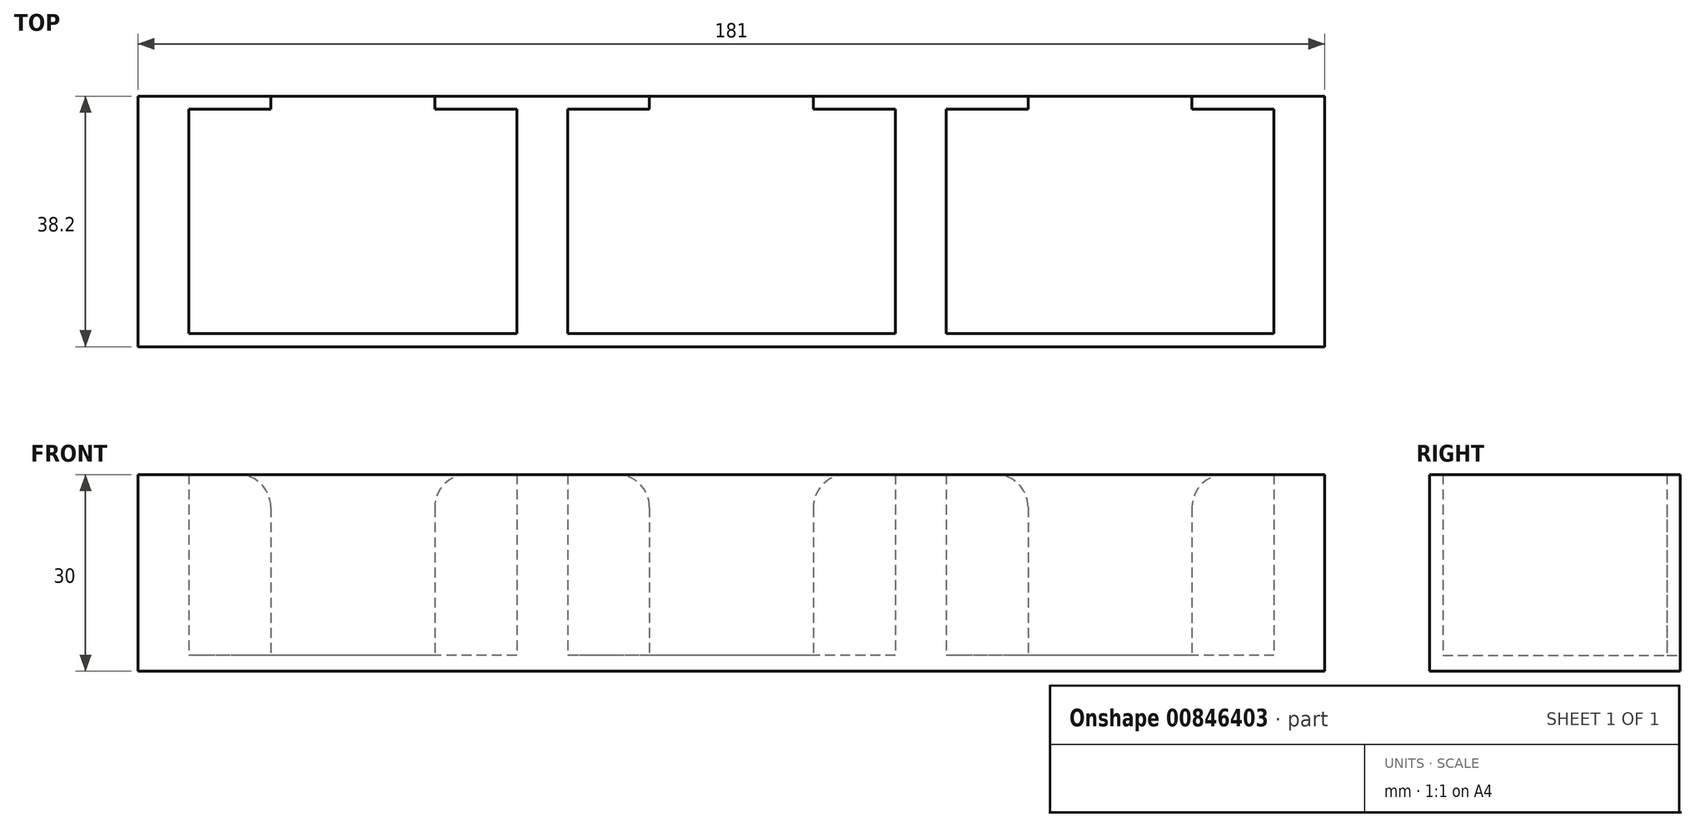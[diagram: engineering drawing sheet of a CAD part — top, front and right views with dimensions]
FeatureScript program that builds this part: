
annotation { "Feature Type Name" : "Feature", "Feature Type Description" : "" }
export const myFeature = defineFeature(function(context is Context, id is Id, definition is map)
    precondition{}
    {
        {
            var Q0;
            Q0=qCreatedBy(makeId("Top.planeOp"),FACE);
            var sketch = newSketch(context, id + "F0", { "sketchPlane" : qUnion([Q0])});
            skPoint(sketch, "E0.middle", {"position": v(0, 0) * mm});
            skLineSegment(sketch, "E1.bottom", {"start": v(90.5, -19.1) * mm, "end": v(-90.5, -19.1) * mm});
            skLineSegment(sketch, "E1.top", {"start": v(90.5, 19.1) * mm, "end": v(-90.5, 19.1) * mm});
            skLineSegment(sketch, "E1.left", {"start": v(90.5, -19.5) * mm, "end": v(90.5, 19.5) * mm});
            skLineSegment(sketch, "E1.right", {"start": v(-90.5, -19.5) * mm, "end": v(-90.5, 19.5) * mm});
            skLineSegment(sketch, "E2.0", {"start": v(88.1, 17.1) * mm, "end": v(-88.1, 17.1) * mm});
            skLineSegment(sketch, "E2.2", {"start": v(88.1, -17.1) * mm, "end": v(-88.1, -17.1) * mm});
            skLineSegment(sketch, "E3.0", {"start": v(82.75, -17.1) * mm, "end": v(82.75, 17.1) * mm});
            skLineSegment(sketch, "E4.0", {"start": v(-82.75, -17.1) * mm, "end": v(-82.75, 17.1) * mm});
            skLineSegment(sketch, "E5.0", {"start": v(-32.75, -17.1) * mm, "end": v(-32.75, 17.1) * mm});
            skLineSegment(sketch, "E6.0", {"start": v(32.75, -17.1) * mm, "end": v(32.75, 17.1) * mm});
            skLineSegment(sketch, "E7.0", {"start": v(-25, -17.1) * mm, "end": v(-25, 17.1) * mm});
            skLineSegment(sketch, "E8.0", {"start": v(25, -17.1) * mm, "end": v(25, 17.1) * mm});
            skLineSegment(sketch, "E9.0", {"start": v(-70.25, -19.5) * mm, "end": v(-70.25, 19.5) * mm});
            skLineSegment(sketch, "E10.0", {"start": v(-45.25, -19.5) * mm, "end": v(-45.25, 19.5) * mm});
            skLineSegment(sketch, "E11.0", {"start": v(-12.5, -19.5) * mm, "end": v(-12.5, 19.5) * mm});
            skLineSegment(sketch, "E12.0", {"start": v(12.5, -19.5) * mm, "end": v(12.5, 19.5) * mm});
            skLineSegment(sketch, "E13.0", {"start": v(45.25, -19.5) * mm, "end": v(45.25, 19.5) * mm});
            skLineSegment(sketch, "E14.0", {"start": v(70.25, -19.5) * mm, "end": v(70.25, 19.5) * mm});
            skSolve(sketch);
        }
        {
            var Q0;
            {var subQ0=sQuery(id+"F0.wireOp",EDGE,"E1.right");Q0=makeQuery(id+"F0.imprint","IMPRINT",FACE,{"disambiguationData":[TD([[makeQuery(id+"F0.imprint","IMPRINT",EDGE,{"derivedFrom":subQ0}),-1.0]])]});}
            var Q1;
            {var subQ0=sQuery(id+"F0.wireOp",EDGE,"E9.0");var subQ1=sQuery(id+"F0.wireOp",EDGE,"E1.bottom");var subQ2=makeQuery(id+"F0.imprint","INTERSECT",VERTEX,{"derivedFrom":[subQ1,subQ0]});Q1=makeQuery(id+"F0.imprint","IMPRINT",FACE,{"disambiguationData":[TD([[makeQuery(id+"F0.imprint","IMPRINT",EDGE,{"disambiguationData":[TD([[subQ2,1.0]])],"derivedFrom":subQ1}),-1.0]])]});}
            var Q2;
            {var subQ2=sQuery(id+"F0.wireOp",EDGE,"E10.0");var subQ7=sQuery(id+"F0.wireOp",EDGE,"E1.bottom");var subQ8=makeQuery(id+"F0.imprint","INTERSECT",VERTEX,{"derivedFrom":[subQ7,subQ2]});Q2=makeQuery(id+"F0.imprint","IMPRINT",FACE,{"disambiguationData":[TD([[makeQuery(id+"F0.imprint","IMPRINT",EDGE,{"disambiguationData":[TD([[subQ8,1.0]])],"derivedFrom":subQ7}),-1.0]])]});}
            var Q3;
            {var subQ2=sQuery(id+"F0.wireOp",EDGE,"E10.0");var subQ7=sQuery(id+"F0.wireOp",EDGE,"E1.top");var subQ8=makeQuery(id+"F0.imprint","INTERSECT",VERTEX,{"derivedFrom":[subQ7,subQ2]});Q3=makeQuery(id+"F0.imprint","IMPRINT",FACE,{"disambiguationData":[TD([[makeQuery(id+"F0.imprint","IMPRINT",EDGE,{"disambiguationData":[TD([[subQ8,1.0]])],"derivedFrom":subQ7}),1.0]])]});}
            var Q4;
            {var subQ0=sQuery(id+"F0.wireOp",EDGE,"E11.0");var subQ1=sQuery(id+"F0.wireOp",EDGE,"E1.bottom");var subQ2=makeQuery(id+"F0.imprint","INTERSECT",VERTEX,{"derivedFrom":[subQ1,subQ0]});Q4=makeQuery(id+"F0.imprint","IMPRINT",FACE,{"disambiguationData":[TD([[makeQuery(id+"F0.imprint","IMPRINT",EDGE,{"disambiguationData":[TD([[subQ2,1.0]])],"derivedFrom":subQ1}),-1.0]])]});}
            var Q5;
            {var subQ2=sQuery(id+"F0.wireOp",EDGE,"E12.0");var subQ4=sQuery(id+"F0.wireOp",EDGE,"E1.bottom");var subQ5=makeQuery(id+"F0.imprint","INTERSECT",VERTEX,{"derivedFrom":[subQ4,subQ2]});Q5=makeQuery(id+"F0.imprint","IMPRINT",FACE,{"disambiguationData":[TD([[makeQuery(id+"F0.imprint","IMPRINT",EDGE,{"disambiguationData":[TD([[subQ5,1.0]])],"derivedFrom":subQ4}),-1.0]])]});}
            var Q6;
            {var subQ0=sQuery(id+"F0.wireOp",EDGE,"E13.0");var subQ1=sQuery(id+"F0.wireOp",EDGE,"E1.bottom");var subQ2=makeQuery(id+"F0.imprint","INTERSECT",VERTEX,{"derivedFrom":[subQ1,subQ0]});Q6=makeQuery(id+"F0.imprint","IMPRINT",FACE,{"disambiguationData":[TD([[makeQuery(id+"F0.imprint","IMPRINT",EDGE,{"disambiguationData":[TD([[subQ2,1.0]])],"derivedFrom":subQ1}),-1.0]])]});}
            var Q7;
            {var subQ6=sQuery(id+"F0.wireOp",EDGE,"E1.left");Q7=makeQuery(id+"F0.imprint","IMPRINT",FACE,{"disambiguationData":[TD([[makeQuery(id+"F0.imprint","IMPRINT",EDGE,{"derivedFrom":subQ6}),1.0]])]});}
            var Q8;
            {var subQ2=sQuery(id+"F0.wireOp",EDGE,"E12.0");var subQ4=sQuery(id+"F0.wireOp",EDGE,"E1.top");var subQ5=makeQuery(id+"F0.imprint","INTERSECT",VERTEX,{"derivedFrom":[subQ4,subQ2]});Q8=makeQuery(id+"F0.imprint","IMPRINT",FACE,{"disambiguationData":[TD([[makeQuery(id+"F0.imprint","IMPRINT",EDGE,{"disambiguationData":[TD([[subQ5,1.0]])],"derivedFrom":subQ4}),1.0]])]});}
            var Q9;
            {var subQ0=sQuery(id+"F0.wireOp",EDGE,"E6.0");Q9=makeQuery(id+"F0.imprint","IMPRINT",FACE,{"disambiguationData":[TD([[makeQuery(id+"F0.imprint","IMPRINT",EDGE,{"derivedFrom":subQ0}),1.0]])]});}
            var Q10;
            {var subQ0=sQuery(id+"F0.wireOp",EDGE,"E5.0");Q10=makeQuery(id+"F0.imprint","IMPRINT",FACE,{"disambiguationData":[TD([[makeQuery(id+"F0.imprint","IMPRINT",EDGE,{"derivedFrom":subQ0}),-1.0]])]});}
            extrude(context, id + "F1", {"entities" : qUnion([Q0, Q1, Q2, Q3, Q4, Q5, Q6, Q7, Q8, Q9, Q10]), "depth" : 30 * mm, "offsetDistance" : 25 * mm});
        }
        {
            var Q0;
            {var subQ0=sQuery(id+"F0.wireOp",EDGE,"E9.0");var subQ1=sQuery(id+"F0.wireOp",EDGE,"E1.top");var subQ2=makeQuery(id+"F0.imprint","INTERSECT",VERTEX,{"derivedFrom":[subQ1,subQ0]});Q0=makeQuery(id+"F0.imprint","IMPRINT",FACE,{"disambiguationData":[TD([[makeQuery(id+"F0.imprint","IMPRINT",EDGE,{"disambiguationData":[TD([[subQ2,1.0]])],"derivedFrom":subQ1}),1.0]])]});}
            var Q1;
            {var subQ0=sQuery(id+"F0.wireOp",EDGE,"E4.0");Q1=makeQuery(id+"F0.imprint","IMPRINT",FACE,{"disambiguationData":[TD([[makeQuery(id+"F0.imprint","IMPRINT",EDGE,{"derivedFrom":subQ0}),-1.0]])]});}
            var Q2;
            {var subQ0=sQuery(id+"F0.wireOp",EDGE,"E10.0");var subQ1=sQuery(id+"F0.wireOp",EDGE,"E2.0");var subQ2=makeQuery(id+"F0.imprint","INTERSECT",VERTEX,{"derivedFrom":[subQ1,subQ0]});Q2=makeQuery(id+"F0.imprint","IMPRINT",FACE,{"disambiguationData":[TD([[makeQuery(id+"F0.imprint","IMPRINT",EDGE,{"disambiguationData":[TD([[subQ2,-1.0]])],"derivedFrom":subQ1}),1.0]])]});}
            var Q3;
            {var subQ0=sQuery(id+"F0.wireOp",EDGE,"E5.0");Q3=makeQuery(id+"F0.imprint","IMPRINT",FACE,{"disambiguationData":[TD([[makeQuery(id+"F0.imprint","IMPRINT",EDGE,{"derivedFrom":subQ0}),1.0]])]});}
            var Q4;
            {var subQ0=sQuery(id+"F0.wireOp",EDGE,"E7.0");Q4=makeQuery(id+"F0.imprint","IMPRINT",FACE,{"disambiguationData":[TD([[makeQuery(id+"F0.imprint","IMPRINT",EDGE,{"derivedFrom":subQ0}),-1.0]])]});}
            var Q5;
            {var subQ0=sQuery(id+"F0.wireOp",EDGE,"E12.0");var subQ1=sQuery(id+"F0.wireOp",EDGE,"E2.0");var subQ2=makeQuery(id+"F0.imprint","INTERSECT",VERTEX,{"derivedFrom":[subQ1,subQ0]});Q5=makeQuery(id+"F0.imprint","IMPRINT",FACE,{"disambiguationData":[TD([[makeQuery(id+"F0.imprint","IMPRINT",EDGE,{"disambiguationData":[TD([[subQ2,-1.0]])],"derivedFrom":subQ1}),1.0]])]});}
            var Q6;
            {var subQ0=sQuery(id+"F0.wireOp",EDGE,"E11.0");var subQ1=sQuery(id+"F0.wireOp",EDGE,"E1.top");var subQ2=makeQuery(id+"F0.imprint","INTERSECT",VERTEX,{"derivedFrom":[subQ1,subQ0]});Q6=makeQuery(id+"F0.imprint","IMPRINT",FACE,{"disambiguationData":[TD([[makeQuery(id+"F0.imprint","IMPRINT",EDGE,{"disambiguationData":[TD([[subQ2,1.0]])],"derivedFrom":subQ1}),1.0]])]});}
            var Q7;
            {var subQ0=sQuery(id+"F0.wireOp",EDGE,"E8.0");Q7=makeQuery(id+"F0.imprint","IMPRINT",FACE,{"disambiguationData":[TD([[makeQuery(id+"F0.imprint","IMPRINT",EDGE,{"derivedFrom":subQ0}),1.0]])]});}
            var Q8;
            {var subQ0=sQuery(id+"F0.wireOp",EDGE,"E6.0");Q8=makeQuery(id+"F0.imprint","IMPRINT",FACE,{"disambiguationData":[TD([[makeQuery(id+"F0.imprint","IMPRINT",EDGE,{"derivedFrom":subQ0}),-1.0]])]});}
            var Q9;
            {var subQ0=sQuery(id+"F0.wireOp",EDGE,"E14.0");var subQ1=sQuery(id+"F0.wireOp",EDGE,"E2.0");var subQ2=makeQuery(id+"F0.imprint","INTERSECT",VERTEX,{"derivedFrom":[subQ1,subQ0]});Q9=makeQuery(id+"F0.imprint","IMPRINT",FACE,{"disambiguationData":[TD([[makeQuery(id+"F0.imprint","IMPRINT",EDGE,{"disambiguationData":[TD([[subQ2,-1.0]])],"derivedFrom":subQ1}),1.0]])]});}
            var Q10;
            {var subQ0=sQuery(id+"F0.wireOp",EDGE,"E13.0");var subQ1=sQuery(id+"F0.wireOp",EDGE,"E1.top");var subQ2=makeQuery(id+"F0.imprint","INTERSECT",VERTEX,{"derivedFrom":[subQ1,subQ0]});Q10=makeQuery(id+"F0.imprint","IMPRINT",FACE,{"disambiguationData":[TD([[makeQuery(id+"F0.imprint","IMPRINT",EDGE,{"disambiguationData":[TD([[subQ2,1.0]])],"derivedFrom":subQ1}),1.0]])]});}
            var Q11;
            {var subQ0=sQuery(id+"F0.wireOp",EDGE,"E3.0");Q11=makeQuery(id+"F0.imprint","IMPRINT",FACE,{"disambiguationData":[TD([[makeQuery(id+"F0.imprint","IMPRINT",EDGE,{"derivedFrom":subQ0}),1.0]])]});}
            extrude(context, id + "F2", {"entities" : qUnion([Q0, Q1, Q2, Q3, Q4, Q5, Q6, Q7, Q8, Q9, Q10, Q11]), "operationType" : NewBodyOperationType.ADD, "depth" : 2.4 * mm, "offsetDistance" : 25 * mm});
        }
        {
            var Q0;
            Q0=makeQuery(id+"F1.opExtrude","CAP_EDGE",EDGE,{"disambiguationData":[OSD([sQuery(id+"F0.wireOp",EDGE,"E9.0")])],"isStart":false});
            var Q1;
            Q1=makeQuery(id+"F1.opExtrude","CAP_EDGE",EDGE,{"disambiguationData":[OSD([sQuery(id+"F0.wireOp",EDGE,"E10.0")])],"isStart":false});
            var Q2;
            Q2=makeQuery(id+"F1.opExtrude","CAP_EDGE",EDGE,{"disambiguationData":[OSD([sQuery(id+"F0.wireOp",EDGE,"E11.0")])],"isStart":false});
            var Q3;
            Q3=makeQuery(id+"F1.opExtrude","CAP_EDGE",EDGE,{"disambiguationData":[OSD([sQuery(id+"F0.wireOp",EDGE,"E12.0")])],"isStart":false});
            var Q4;
            Q4=makeQuery(id+"F1.opExtrude","CAP_EDGE",EDGE,{"disambiguationData":[OSD([sQuery(id+"F0.wireOp",EDGE,"E13.0")])],"isStart":false});
            var Q5;
            Q5=makeQuery(id+"F1.opExtrude","CAP_EDGE",EDGE,{"disambiguationData":[OSD([sQuery(id+"F0.wireOp",EDGE,"E14.0")])],"isStart":false});
            fillet(context, id + "F3", {"entities" : qUnion([Q0, Q1, Q2, Q3, Q4, Q5]), "radius" : 5 * mm, "tangentPropagation" : true, "allowEdgeOverflow" : false});
        }
    });
